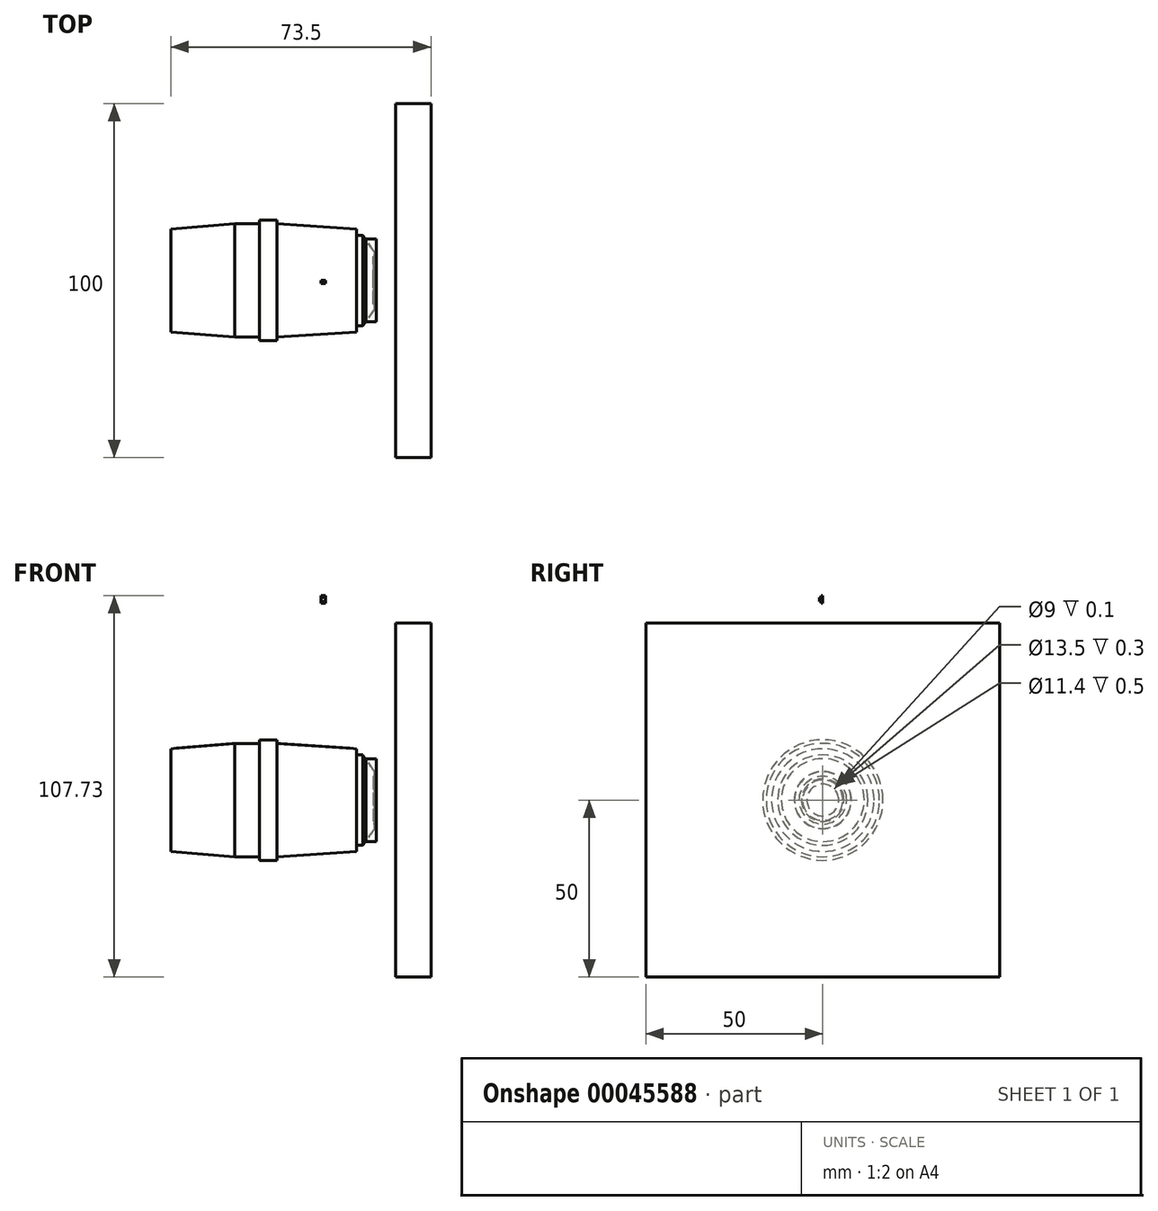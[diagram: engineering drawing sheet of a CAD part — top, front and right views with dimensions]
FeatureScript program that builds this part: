
annotation { "Feature Type Name" : "Feature", "Feature Type Description" : "" }
export const myFeature = defineFeature(function(context is Context, id is Id, definition is map)
    precondition{}
    {
        {
            var Q0;
            Q0=qCreatedBy(makeId("Front.planeOp"),FACE);
            var sketch = newSketch(context, id + "F0", { "sketchPlane" : qUnion([Q0])});
            skLineSegment(sketch, "E0", {"start": v(0, 0) * mm, "end": v(0, 14.5) * mm});
            skLineSegment(sketch, "E1", {"start": v(57.5, 6) * mm, "end": v(57.2, 6) * mm});
            skLineSegment(sketch, "E2", {"start": v(57.5, 6) * mm, "end": v(57.5, 4.5) * mm});
            skLineSegment(sketch, "E3", {"start": v(57.5, 4.5) * mm, "end": v(57.4, 4.5) * mm});
            skLineSegment(sketch, "E4", {"start": v(57.4, 4.5) * mm, "end": v(57.4, 0) * mm});
            skLineSegment(sketch, "E5", {"start": v(57.4, 0) * mm, "end": v(0, 0) * mm});
            skLineSegment(sketch, "E6", {"start": v(57.2, 6) * mm, "end": v(57.2, 6.75) * mm});
            skLineSegment(sketch, "E7", {"start": v(57.2, 6.75) * mm, "end": v(57.5, 6.75) * mm});
            skLineSegment(sketch, "E8", {"start": v(57.5, 6.75) * mm, "end": v(57.5, 8) * mm});
            skLineSegment(sketch, "E9", {"start": v(57.5, 8) * mm, "end": v(54.2, 12.75) * mm});
            skLineSegment(sketch, "E10", {"start": v(54.2, 12.75) * mm, "end": v(52.5, 12.75) * mm});
            skLineSegment(sketch, "E11", {"start": v(52.5, 12.75) * mm, "end": v(52.5, 14.5) * mm});
            skLineSegment(sketch, "E12", {"start": v(52.5, 14.5) * mm, "end": v(30, 16) * mm});
            skLineSegment(sketch, "E13", {"start": v(25, 16) * mm, "end": v(18, 16) * mm});
            skLineSegment(sketch, "E14", {"start": v(18, 16) * mm, "end": v(0, 14.5) * mm});
            skLineSegment(sketch, "E15", {"start": v(30, 16) * mm, "end": v(30, 17) * mm});
            skLineSegment(sketch, "E16", {"start": v(30, 17) * mm, "end": v(25, 17) * mm});
            skLineSegment(sketch, "E17", {"start": v(25, 17) * mm, "end": v(25, 16) * mm});
            skSolve(sketch);
        }
        {
            var Q0;
            Q0=qCreatedBy(makeId("Front.planeOp"),FACE);
            var sketch = newSketch(context, id + "F1", { "sketchPlane" : qUnion([Q0])});
            skLineSegment(sketch, "E18", {"start": v(-13.48, 0) * mm, "end": v(73.81, 0) * mm, "construction": true});
            skSolve(sketch);
        }
        {
            var Q0;
            Q0=qSketchRegion(id+"F0",true);
            var Q1;
            Q1=sQuery(id+"F1.wireOp",EDGE,"E18");
            revolve(context, id + "F2", {"entities" : qUnion([Q0]), "axis" : qUnion([Q1]), "revolveType" : RevolveType.FULL});
        }
        {
            var Q0;
            Q0=qCreatedBy(makeId("Top.planeOp"),FACE);
            var sketch = newSketch(context, id + "F3", { "sketchPlane" : qUnion([Q0])});
            skLineSegment(sketch, "E19.bottom", {"start": v(63.5, 50) * mm, "end": v(73.5, 50) * mm});
            skLineSegment(sketch, "E19.top", {"start": v(63.5, -50) * mm, "end": v(73.5, -50) * mm});
            skLineSegment(sketch, "E19.left", {"start": v(63.5, 50) * mm, "end": v(63.5, -50) * mm});
            skLineSegment(sketch, "E19.right", {"start": v(73.5, 50) * mm, "end": v(73.5, -50) * mm});
            skSolve(sketch);
        }
        {
            var Q0;
            Q0=qSketchRegion(id+"F3",true);
            extrude(context, id + "F4", {"entities" : qUnion([Q0]), "endBound" : BoundingType.SYMMETRIC, "depth" : 100 * mm});
        }
        {
            var Q0;
            Q0=qCreatedBy(makeId("Front.planeOp"),FACE);
            var sketch = newSketch(context, id + "F5", { "sketchPlane" : qUnion([Q0])});
            skLineSegment(sketch, "E20", {"start": v(57.6, 5.7) * mm, "end": v(57.6, 8.1) * mm});
            skLineSegment(sketch, "E21", {"start": v(57.6, 8.1) * mm, "end": v(55.1, 11.7) * mm});
            skLineSegment(sketch, "E22", {"start": v(55.1, 11.7) * mm, "end": v(58.1, 11.7) * mm});
            skLineSegment(sketch, "E23", {"start": v(58.1, 11.7) * mm, "end": v(58.1, 5.7) * mm});
            skLineSegment(sketch, "E24", {"start": v(58.1, 5.7) * mm, "end": v(57.6, 5.7) * mm});
            skLineSegment(sketch, "E25", {"start": v(60.04, 0) * mm, "end": v(48.15, 0) * mm, "construction": true});
            skSolve(sketch);
        }
        {
            var Q0;
            Q0=qSketchRegion(id+"F5",true);
            var Q1;
            Q1=sQuery(id+"F5.wireOp",EDGE,"E25");
            revolve(context, id + "F6", {"entities" : qUnion([Q0]), "axis" : qUnion([Q1]), "revolveType" : RevolveType.FULL});
        }
        {
            var Q0;
            Q0=qCreatedBy(makeId("Front.planeOp"),FACE);
            var sketch = newSketch(context, id + "F7", { "sketchPlane" : qUnion([Q0])});
            skLineSegment(sketch, "E26.bottom", {"start": v(42.38, 57.73) * mm, "end": v(43.73, 57.73) * mm});
            skLineSegment(sketch, "E26.top", {"start": v(42.38, 55.63) * mm, "end": v(43.73, 55.63) * mm});
            skLineSegment(sketch, "E26.left", {"start": v(42.38, 57.73) * mm, "end": v(42.38, 55.63) * mm});
            skLineSegment(sketch, "E26.right", {"start": v(43.73, 57.73) * mm, "end": v(43.73, 55.63) * mm});
            skSolve(sketch);
        }
        {
            var Q0;
            Q0=qSketchRegion(id+"F7",true);
            extrude(context, id + "F8", {"entities" : qUnion([Q0]), "depth" : .4 * mm});
        }
        {
            var Q0;
            Q0=makeQuery(id+"F8.opExtrude","CAP_FACE",FACE,{"disambiguationData":[OSD([sQuery(id+"F7.wireOp",EDGE,"E26.bottom"),sQuery(id+"F7.wireOp",EDGE,"E26.top"),sQuery(id+"F7.wireOp",EDGE,"E26.left"),sQuery(id+"F7.wireOp",EDGE,"E26.right")])],"isStart":false});
            var sketch = newSketch(context, id + "F9", { "sketchPlane" : qUnion([Q0])});
            skLineSegment(sketch, "E27.bottom", {"start": v(42.38, 57.28) * mm, "end": v(43.73, 57.28) * mm});
            skLineSegment(sketch, "E27.top", {"start": v(42.38, 56.08) * mm, "end": v(43.73, 56.08) * mm});
            skLineSegment(sketch, "E27.left", {"start": v(42.38, 57.28) * mm, "end": v(42.38, 56.08) * mm});
            skLineSegment(sketch, "E27.right", {"start": v(43.73, 57.28) * mm, "end": v(43.73, 56.08) * mm});
            skSolve(sketch);
        }
        {
            var Q0;
            Q0=qSketchRegion(id+"F9",true);
            extrude(context, id + "F10", {"entities" : qUnion([Q0]), "operationType" : NewBodyOperationType.ADD, "depth" : .5 * mm});
        }
    });
